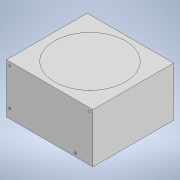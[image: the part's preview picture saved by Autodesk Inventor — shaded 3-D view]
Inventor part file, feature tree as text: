
AUTODESK INVENTOR PART (.ipt)
format: ipt  version: 2021 (Build 250183000, 183)  size: 125,952 bytes
history: native  units: in
note: dims shown in document units (in); Inventor stores cm internally (conversion verified against a paired STEP export)
features: extrude x3, sketch x3
ambient origin geometry x8: Origin, YZ Plane, XZ Plane, XY Plane, X Axis, Y Axis, Z Axis, Center Point
bodies: Solid1 (feature_tree)
feature tree (6):
  extrude  "Extrusion1"  Depth=5.9055in
  extrude  "Extrusion2"  Depth=3.3858in
  extrude  "Extrusion3"  Depth=0.0004in
  sketch  "Sketch1"  dims[d0=5.5118in d2=5.9055in]
  sketch  "Sketch2"  dims[d3=3.3858in d4=0.0in d5=0.2362in]
  sketch  "Sketch3"  dims[d6=0.6299in d7=2.5197in d8=5.4331in d9=360.0deg d10=0.2362in d11=4.4882in d12=2.9134in d13=0.1378in d14=0.1378in d15=0.1378in d16=0.1378in d17=0.1875in d18=0.0in d19=2.7559in d20=5.5118in d21=5.9055in d22=2.9528in d23=0.0004in d24=0.0in]
